# Revit family: BSC-Class-II_Type-A2_NuAire_BioSafetyCab_602
name_source: partatom
category: Mechanical Equipment
units: mm (PartAtom-declared; Revit-internal decimal feet)

## family parameters
Always vertical = Yes
Classification Number = 23.40.70.11.11.11.11
Cut with Voids When Loaded = No
Maintain Annotation Orientation = No
Part Type = Normal
Room Calculation Point = No
Round Connector Dimension = Use Diameter
Shared = No
Work Plane-Based = No

## types (3) — shared parameters
Assembly Code = E1020720
Construction Details = http://www.arcat.com
DEPTH = 2' - 6 1/4"
Default Elevation = 0' - 0"
Description = Class II Type A2 Biological Safety Cabinet
HEIGHT = 5' - 8 5/8"
Keynote = 11 53 00
Manufacturer = Nuaire Inc
Manufacturer Fax = 763-553-0459
Manufacturer Website = http://www.nuaire.com
Product Data = http://www.arcat.com
Product Properties = http://www.nuaire.com
Revision = R1_12/2015
Sales Information = http://www.nuaire.com
Specification = http://www.arcat.com
URL = http://www.nuaire.com
Workzone depth = 2' - 0 1/2"

## per-type parameters (varying)
| type | EXHAUST SIDE | EXHAUST WIDTH | WIDTH | WORK SURFACE HEIGHT |
| NU-602-400 | 0' - 4 3/4" | 2' - 8" | 4' - 2 1/2" | 2' - 7" |
| NU-602-500 | 0' - 9 1/4" | 3' - 2" | 5' - 2 1/2" | 2' - 6 27/32" |
| NU-602-600 | 1' - 3 1/4" | 3' - 7 15/16" | 6' - 2 1/2" | 2' - 6 27/32" |

note: column(s) folded — value = type name in every type: Model

## geometry (parser evidence)
native form markers: Blend x2, Sweep x3
no freeform markers — native parametric forms only
